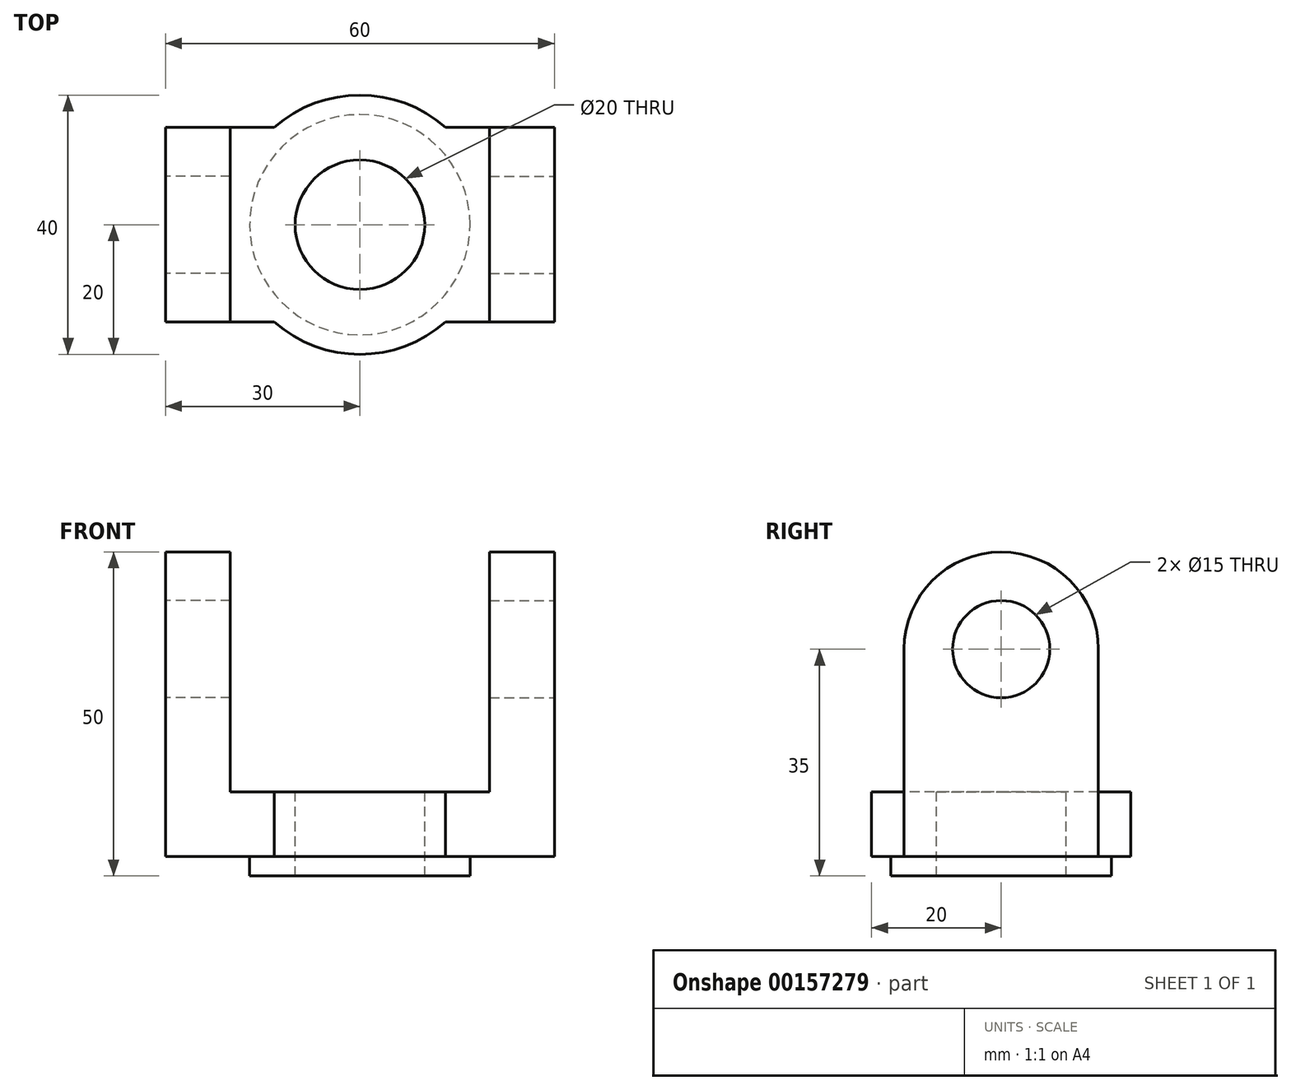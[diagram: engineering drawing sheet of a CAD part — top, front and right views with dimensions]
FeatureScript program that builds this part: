
annotation { "Feature Type Name" : "Feature", "Feature Type Description" : "" }
export const myFeature = defineFeature(function(context is Context, id is Id, definition is map)
    precondition{}
    {
        {
            var Q0;
            Q0=qCreatedBy(makeId("Top.planeOp"),FACE);
            var sketch = newSketch(context, id + "F0", { "sketchPlane" : qUnion([Q0])});
            skArc(sketch, "E0", {"start": v(-13.23, -15) * mm, "mid": v(0, -20) * mm, "end": v(13.23, -15) * mm});
            skLineSegment(sketch, "E1.bottom", {"start": v(30, 15) * mm, "end": v(13.23, 15) * mm});
            skLineSegment(sketch, "E1.top", {"start": v(30, -15) * mm, "end": v(13.23, -15) * mm});
            skLineSegment(sketch, "E1.left", {"start": v(30, 15) * mm, "end": v(30, -15) * mm});
            skLineSegment(sketch, "E1.right", {"start": v(-30, 15) * mm, "end": v(-30, -15) * mm});
            skPoint(sketch, "E2", {"position": v(-13.23, 15) * mm});
            skPoint(sketch, "E3", {"position": v(13.23, 15) * mm});
            skPoint(sketch, "E4", {"position": v(13.23, -15) * mm});
            skPoint(sketch, "E5", {"position": v(-13.23, -15) * mm});
            skLineSegment(sketch, "E6.trimOffspring", {"start": v(-13.23, -15) * mm, "end": v(-30, -15) * mm});
            skArc(sketch, "E7.trimOffspring", {"start": v(13.23, 15) * mm, "mid": v(0, 20) * mm, "end": v(-13.23, 15) * mm});
            skLineSegment(sketch, "E8.trimOffspring", {"start": v(-13.23, 15) * mm, "end": v(-30, 15) * mm});
            skSolve(sketch);
        }
        {
            var Q0;
            Q0 = qSketchRegion(id + "F0", true);
            extrude(context, id + "F1", {"entities" : qUnion([Q0]), "oppositeDirection" : true, "depth" : 10 * mm});
        }
        {
            var Q0;
            Q0=makeQuery(id+"F1.opExtrude","CAP_FACE",FACE,{"disambiguationData":[OSD([sQuery(id+"F0.wireOp",EDGE,"E0"),sQuery(id+"F0.wireOp",EDGE,"E1.bottom"),sQuery(id+"F0.wireOp",EDGE,"E1.top"),sQuery(id+"F0.wireOp",EDGE,"E1.left"),sQuery(id+"F0.wireOp",EDGE,"E1.right"),sQuery(id+"F0.wireOp",EDGE,"E6.trimOffspring"),sQuery(id+"F0.wireOp",EDGE,"E7.trimOffspring"),sQuery(id+"F0.wireOp",EDGE,"E8.trimOffspring")])],"isStart":false});
            var sketch = newSketch(context, id + "F2", { "sketchPlane" : qUnion([Q0])});
            skCircle(sketch, "E9", {"center": v(0, 0) * mm, "radius": 17 * mm});
            skSolve(sketch);
        }
        {
            var Q0;
            Q0 = qSketchRegion(id + "F2", true);
            extrude(context, id + "F3", {"entities" : qUnion([Q0]), "operationType" : NewBodyOperationType.ADD, "depth" : 3 * mm});
        }
        {
            var Q0;
            Q0=makeQuery(id+"F1.opExtrude","CAP_FACE",FACE,{"disambiguationData":[OSD([sQuery(id+"F0.wireOp",EDGE,"E0"),sQuery(id+"F0.wireOp",EDGE,"E1.bottom"),sQuery(id+"F0.wireOp",EDGE,"E1.top"),sQuery(id+"F0.wireOp",EDGE,"E1.left"),sQuery(id+"F0.wireOp",EDGE,"E1.right"),sQuery(id+"F0.wireOp",EDGE,"E6.trimOffspring"),sQuery(id+"F0.wireOp",EDGE,"E7.trimOffspring"),sQuery(id+"F0.wireOp",EDGE,"E8.trimOffspring")])],"isStart":true});
            var sketch = newSketch(context, id + "F4", { "sketchPlane" : qUnion([Q0])});
            skCircle(sketch, "E10", {"center": v(0, 0) * mm, "radius": 10 * mm});
            skSolve(sketch);
        }
        {
            var Q0;
            Q0 = qSketchRegion(id + "F4", true);
            extrude(context, id + "F5", {"entities" : qUnion([Q0]), "operationType" : NewBodyOperationType.REMOVE, "endBound" : BoundingType.THROUGH_ALL, "oppositeDirection" : true, "depth" : 25 * mm});
        }
        {
            var Q0;
            Q0=makeQuery(id+"F1.opExtrude","SWEPT_FACE",FACE,{"disambiguationData":[OSD([sQuery(id+"F0.wireOp",EDGE,"E1.left")])]});
            var sketch = newSketch(context, id + "F6", { "sketchPlane" : qUnion([Q0])});
            skLineSegment(sketch, "E11.0", {"start": v(15, 0) * mm, "end": v(-15, 0) * mm});
            skLineSegment(sketch, "E12", {"start": v(-15, 0) * mm, "end": v(-15, 22) * mm});
            skLineSegment(sketch, "E13", {"start": v(15, 0) * mm, "end": v(15, 22) * mm});
            skCircle(sketch, "E14", {"center": v(0, 22) * mm, "radius": 7.5 * mm});
            skLineSegment(sketch, "E15.0", {"start": v(17, -13) * mm, "end": v(-17, -13) * mm});
            skArc(sketch, "E16", {"start": v(-15, 22) * mm, "mid": v(0, 37) * mm, "end": v(15, 22) * mm});
            skSolve(sketch);
        }
        {
            var Q0;
            Q0 = qSketchRegion(id + "F6", true);
            extrude(context, id + "F7", {"entities" : qUnion([Q0]), "operationType" : NewBodyOperationType.ADD, "oppositeDirection" : true, "depth" : 10 * mm});
        }
        {
            var Q0;
            Q0=makeQuery(id+"F1.opExtrude","SWEPT_FACE",FACE,{"disambiguationData":[OSD([sQuery(id+"F0.wireOp",EDGE,"E1.right")])]});
            var sketch = newSketch(context, id + "F8", { "sketchPlane" : qUnion([Q0])});
            skLineSegment(sketch, "E17.0", {"start": v(-15, 0) * mm, "end": v(15, 0) * mm});
            skLineSegment(sketch, "E18.0", {"start": v(-15, 0) * mm, "end": v(-15, 22) * mm});
            skArc(sketch, "E19.0", {"start": v(15, 22) * mm, "mid": v(0, 37) * mm, "end": v(-15, 22) * mm});
            skLineSegment(sketch, "E20.0", {"start": v(15, -10) * mm, "end": v(15, 22) * mm});
            skCircle(sketch, "E21.0", {"center": v(0, 22) * mm, "radius": 7.5 * mm});
            skSolve(sketch);
        }
        {
            var Q0;
            Q0 = qSketchRegion(id + "F8", true);
            extrude(context, id + "F9", {"entities" : qUnion([Q0]), "operationType" : NewBodyOperationType.ADD, "oppositeDirection" : true, "depth" : 10 * mm});
        }
    });
